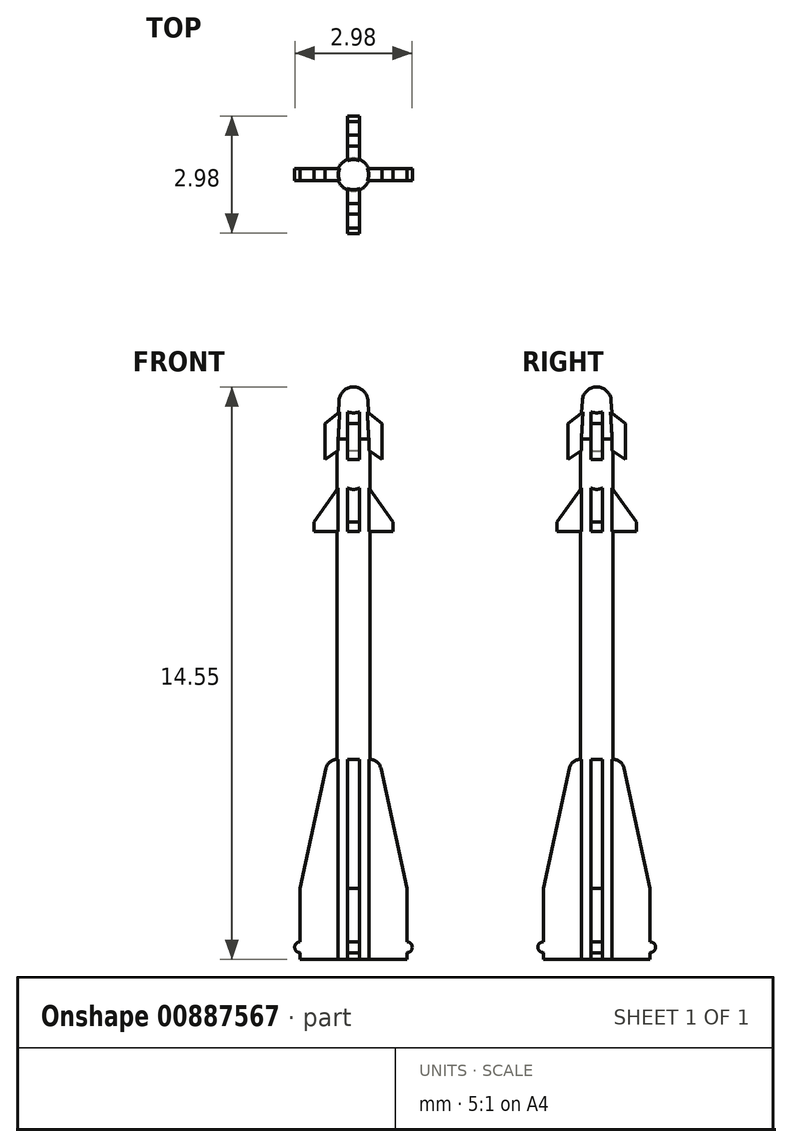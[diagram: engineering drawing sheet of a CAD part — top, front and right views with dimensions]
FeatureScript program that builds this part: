
annotation { "Feature Type Name" : "Feature", "Feature Type Description" : "" }
export const myFeature = defineFeature(function(context is Context, id is Id, definition is map)
    precondition{}
    {
        {
            var Q0;
            Q0=qCreatedBy(makeId("Front.planeOp"),FACE);
            var sketch = newSketch(context, id + "F0", { "sketchPlane" : qUnion([Q0])});
            skLineSegment(sketch, "E0", {"start": v(0, 0) * mm, "end": v(0, 14.55) * mm});
            skLineSegment(sketch, "E1", {"start": v(0.42, 13.23) * mm, "end": v(0.42, 0) * mm});
            skLineSegment(sketch, "E2", {"start": v(0.42, 0) * mm, "end": v(0, 0) * mm});
            skLineSegment(sketch, "E3", {"start": v(0.42, 13.23) * mm, "end": v(0.37, 14.2) * mm});
            skArc(sketch, "E4", {"start": v(0.37, 14.2) * mm, "mid": v(0.25, 14.45) * mm, "end": v(0, 14.55) * mm});
            skLineSegment(sketch, "E5", {"start": v(0, 14.55) * mm, "end": v(-0.14, 14.55) * mm, "construction": true});
            skSolve(sketch);
        }
        {
            var Q0;
            Q0=makeQuery(id+"F0.imprint","IMPRINT",FACE,{"disambiguationData":[TD([[makeQuery(id+"F0.imprint","IMPRINT",EDGE,{"derivedFrom":sQuery(id+"F0.wireOp",EDGE,"E0")}),-1.0]])]});
            var Q1;
            Q1=sQuery(id+"F0.wireOp",EDGE,"E0");
            revolve(context, id + "F1", {"surfaceOperationType" : NewSurfaceOperationType.NEW, "entities" : qUnion([Q0]), "axis" : qUnion([Q1]), "revolveType" : RevolveType.FULL});
        }
        {
            var Q0;
            Q0=qCreatedBy(makeId("Front.planeOp"),FACE);
            var sketch = newSketch(context, id + "F2", { "sketchPlane" : qUnion([Q0])});
            skLineSegment(sketch, "E6.0", {"start": v(0.42, 13.23) * mm, "end": v(-0.42, 13.23) * mm, "construction": true});
            skLineSegment(sketch, "E7", {"start": v(0, 0) * mm, "end": v(1.35, 0) * mm});
            skLineSegment(sketch, "E8", {"start": v(1.35, 1.8) * mm, "end": v(0.7, 4.86) * mm});
            skLineSegment(sketch, "E9", {"start": v(0.2, 5.09) * mm, "end": v(0.2, 10.87) * mm});
            skLineSegment(sketch, "E10", {"start": v(0.2, 10.87) * mm, "end": v(1, 10.87) * mm});
            skLineSegment(sketch, "E11", {"start": v(0, 14.2) * mm, "end": v(0, 0) * mm});
            skLineSegment(sketch, "E12", {"start": v(0.42, 13.23) * mm, "end": v(0.42, 0) * mm, "construction": true});
            skLineSegment(sketch, "E13", {"start": v(1.35, 0) * mm, "end": v(1.35, 0.17) * mm});
            skLineSegment(sketch, "E14", {"start": v(1, 10.87) * mm, "end": v(1, 11.11) * mm});
            skLineSegment(sketch, "E15", {"start": v(0.2, 12.25) * mm, "end": v(0.2, 13.06) * mm});
            skLineSegment(sketch, "E16", {"start": v(0.73, 12.7) * mm, "end": v(0.2, 13.06) * mm});
            skLineSegment(sketch, "E17", {"start": v(0.73, 12.7) * mm, "end": v(0.73, 13.61) * mm});
            skLineSegment(sketch, "E18", {"start": v(0.73, 13.61) * mm, "end": v(0, 14.2) * mm});
            skLineSegment(sketch, "E19", {"start": v(1, 11.11) * mm, "end": v(0.2, 12.25) * mm});
            skPoint(sketch, "E20", {"position": v(0.42, 11.94) * mm});
            skPoint(sketch, "E21", {"position": v(0.42, 12.92) * mm});
            skArc(sketch, "E22", {"start": v(0.7, 4.86) * mm, "mid": v(0.6, 5.02) * mm, "end": v(0.42, 5.09) * mm});
            skLineSegment(sketch, "E23", {"start": v(0.2, 5.09) * mm, "end": v(0.42, 5.09) * mm});
            skLineSegment(sketch, "E24.0", {"start": v(0.37, 14.2) * mm, "end": v(-0.37, 14.2) * mm, "construction": true});
            skLineSegment(sketch, "E25", {"start": v(0.37, 14.2) * mm, "end": v(0.42, 13.23) * mm, "construction": true});
            skPoint(sketch, "E26", {"position": v(0.38, 13.89) * mm});
            skArc(sketch, "E27", {"start": v(1.35, 0.17) * mm, "mid": v(1.5, 0.31) * mm, "end": v(1.35, 0.45) * mm});
            skLineSegment(sketch, "E28.trimOffspring", {"start": v(1.35, 0.45) * mm, "end": v(1.35, 1.8) * mm});
            skSolve(sketch);
        }
        {
            var Q0;
            Q0=qSketchRegion(id+"F2",true);
            extrude(context, id + "F3", {"entities" : qUnion([Q0]), "operationType" : NewBodyOperationType.ADD, "oppositeDirection" : true, "depth" : .3 * mm, "offsetDistance" : 25 * mm, "symmetric" : true});
        }
        {
            var Q0;
            Q0=makeQuery(id+"F1.opRevolve","SWEPT_BODY",BODY,{"disambiguationData":[OSD([sQuery(id+"F0.wireOp",EDGE,"E0"),sQuery(id+"F0.wireOp",EDGE,"E1"),sQuery(id+"F0.wireOp",EDGE,"E2"),sQuery(id+"F0.wireOp",EDGE,"h1jDSi8t-veb7-85qg-XgDk-6E8DmZjBuz4r")])]});
            var Q1;
            Q1=makeQuery(id+"F1.opRevolve","SWEPT_FACE",FACE,{"disambiguationData":[OSD([sQuery(id+"F0.wireOp",EDGE,"E1")])]});
            circularPattern(context, id + "F4", {"operationType" : NewBodyOperationType.ADD, "entities" : qUnion([Q0]), "axis" : qUnion([Q1]), "angle" : 360 * degree, "instanceCount" : 4, "equalSpace" : true, "computeTransformsWithoutBuiltin" : true});
        }
    });
